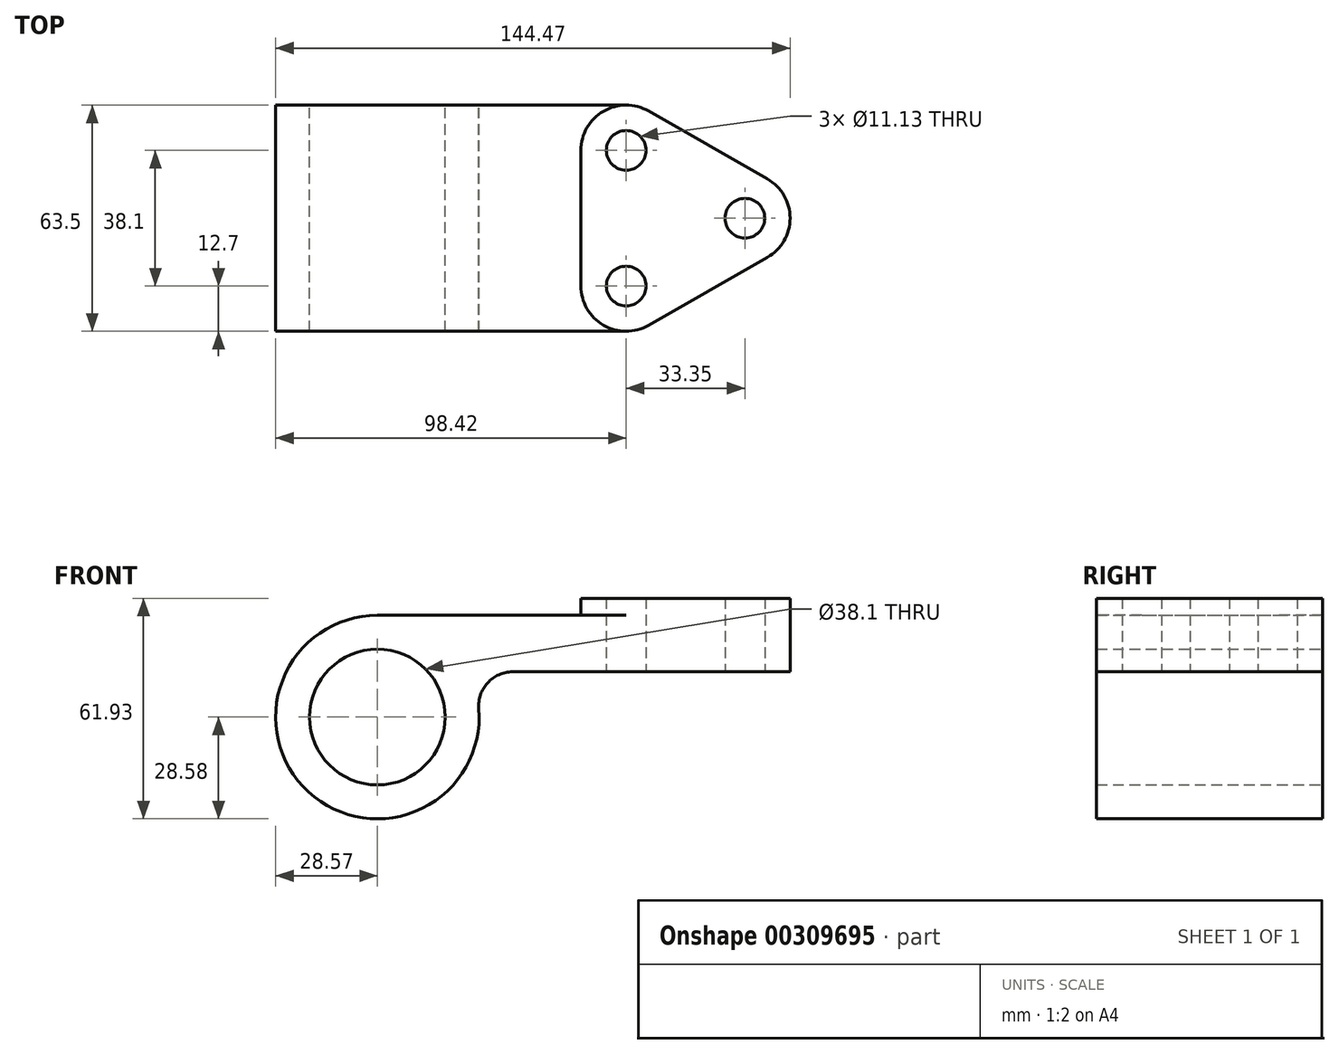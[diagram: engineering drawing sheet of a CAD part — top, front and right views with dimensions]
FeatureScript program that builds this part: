
annotation { "Feature Type Name" : "Feature", "Feature Type Description" : "" }
export const myFeature = defineFeature(function(context is Context, id is Id, definition is map)
    precondition{}
    {
        {
            var Q0;
            Q0=qCreatedBy(makeId("Front.planeOp"),FACE);
            var sketch = newSketch(context, id + "F0", { "sketchPlane" : qUnion([Q0])});
            skCircle(sketch, "E0", {"center": v(0, 0) * mm, "radius": 19.05 * mm});
            skArc(sketch, "E1", {"start": v(0, 28.58) * mm, "mid": v(-19.35, -21.03) * mm, "end": v(28.48, 2.38) * mm});
            skLineSegment(sketch, "E2", {"start": v(0, 28.58) * mm, "end": v(69.85, 28.58) * mm});
            skArc(sketch, "E3", {"start": v(37.97, 12.7) * mm, "mid": v(30.96, 9.62) * mm, "end": v(28.48, 2.38) * mm});
            skPoint(sketch, "E4.endSnap0", {"position": v(63.76, 12.7) * mm});
            skLineSegment(sketch, "E5", {"start": v(37.97, 12.7) * mm, "end": v(69.85, 12.7) * mm});
            skLineSegment(sketch, "E6", {"start": v(69.85, 12.7) * mm, "end": v(69.85, 28.58) * mm});
            skSolve(sketch);
        }
        {
            var Q0;
            Q0 = qSketchRegion(id + "F0", true);
            extrude(context, id + "F1", {"entities" : qUnion([Q0]), "depth" : 63.5 * mm});
        }
        {
            var Q0;
            Q0=makeQuery(id+"F1.opExtrude","SWEPT_FACE",FACE,{"disambiguationData":[OSD([sQuery(id+"F0.wireOp",EDGE,"E2")])]});
            var sketch = newSketch(context, id + "F2", { "sketchPlane" : qUnion([Q0])});
            skLineSegment(sketch, "E7", {"start": v(57.15, -12.7) * mm, "end": v(57.15, -50.8) * mm});
            skArc(sketch, "E8", {"start": v(57.15, -50.8) * mm, "mid": v(63.47, -61.78) * mm, "end": v(76.15, -61.83) * mm});
            skArc(sketch, "E9", {"start": v(76.15, -1.67) * mm, "mid": v(63.47, -1.72) * mm, "end": v(57.15, -12.7) * mm});
            skLineSegment(sketch, "E10", {"start": v(109.5, -20.72) * mm, "end": v(76.15, -1.67) * mm});
            skLineSegment(sketch, "E11", {"start": v(76.15, -61.83) * mm, "end": v(109.5, -42.78) * mm});
            skArc(sketch, "E12", {"start": v(109.5, -42.78) * mm, "mid": v(115.9, -31.75) * mm, "end": v(109.5, -20.72) * mm});
            skPoint(sketch, "E13", {"position": v(69.85, -63.5) * mm});
            skPoint(sketch, "E14.positionSnap0", {"position": v(63.47, -1.72) * mm});
            skPoint(sketch, "E15", {"position": v(69.85, 0) * mm});
            skCircle(sketch, "E16", {"center": v(69.85, -12.7) * mm, "radius": 5.56 * mm});
            skCircle(sketch, "E17", {"center": v(103.2, -31.75) * mm, "radius": 5.56 * mm});
            skCircle(sketch, "E18", {"center": v(69.85, -50.8) * mm, "radius": 5.56 * mm});
            skSolve(sketch);
        }
        {
            var Q0;
            Q0 = qSketchRegion(id + "F2", true);
            extrude(context, id + "F3", {"entities" : qUnion([Q0]), "operationType" : NewBodyOperationType.ADD, "depth" : 4.78 * mm, "hasSecondDirection" : true, "secondDirectionOppositeDirection" : true, "secondDirectionDepth" : 15.88 * mm});
        }
        {
            var Q0;
            Q0=makeQuery(id+"F3.boolean.opBoolean","SPLIT",FACE,{"disambiguationData":[TD([makeQuery(id+"F3.opExtrude","SWEPT_FACE",FACE,{"disambiguationData":[OSD([sQuery(id+"F2.wireOp",EDGE,"E16")])]})])],"derivedFrom":makeQuery(id+"F1.opExtrude","SWEPT_FACE",FACE,{"disambiguationData":[OSD([sQuery(id+"F0.wireOp",EDGE,"E2")])]})});
            var sketch = newSketch(context, id + "F4", { "sketchPlane" : qUnion([Q0])});
            skArc(sketch, "E19", {"start": v(69.85, -7.14) * mm, "mid": v(64.29, -12.7) * mm, "end": v(69.85, -18.26) * mm});
            skArc(sketch, "E20", {"start": v(69.85, -45.24) * mm, "mid": v(64.29, -50.8) * mm, "end": v(69.85, -56.36) * mm});
            skLineSegment(sketch, "E21", {"start": v(69.85, -18.26) * mm, "end": v(69.85, -7.14) * mm});
            skLineSegment(sketch, "E22", {"start": v(69.85, -45.24) * mm, "end": v(69.85, -56.36) * mm});
            skSolve(sketch);
        }
        {
            var Q0;
            Q0=makeQuery(id+"F4.imprint","IMPRINT",FACE,{"disambiguationData":[TD([[makeQuery(id+"F4.imprint","IMPRINT",EDGE,{"derivedFrom":sQuery(id+"F4.wireOp",EDGE,"E19")}),-1.0]])]});
            var Q1;
            Q1=makeQuery(id+"F4.imprint","IMPRINT",FACE,{"disambiguationData":[TD([[makeQuery(id+"F4.imprint","IMPRINT",EDGE,{"derivedFrom":sQuery(id+"F4.wireOp",EDGE,"E20")}),1.0]])]});
            extrude(context, id + "F5", {"entities" : qUnion([Q0, Q1]), "operationType" : NewBodyOperationType.REMOVE, "endBound" : BoundingType.THROUGH_ALL, "oppositeDirection" : true, "depth" : 25.4 * mm});
        }
    });
